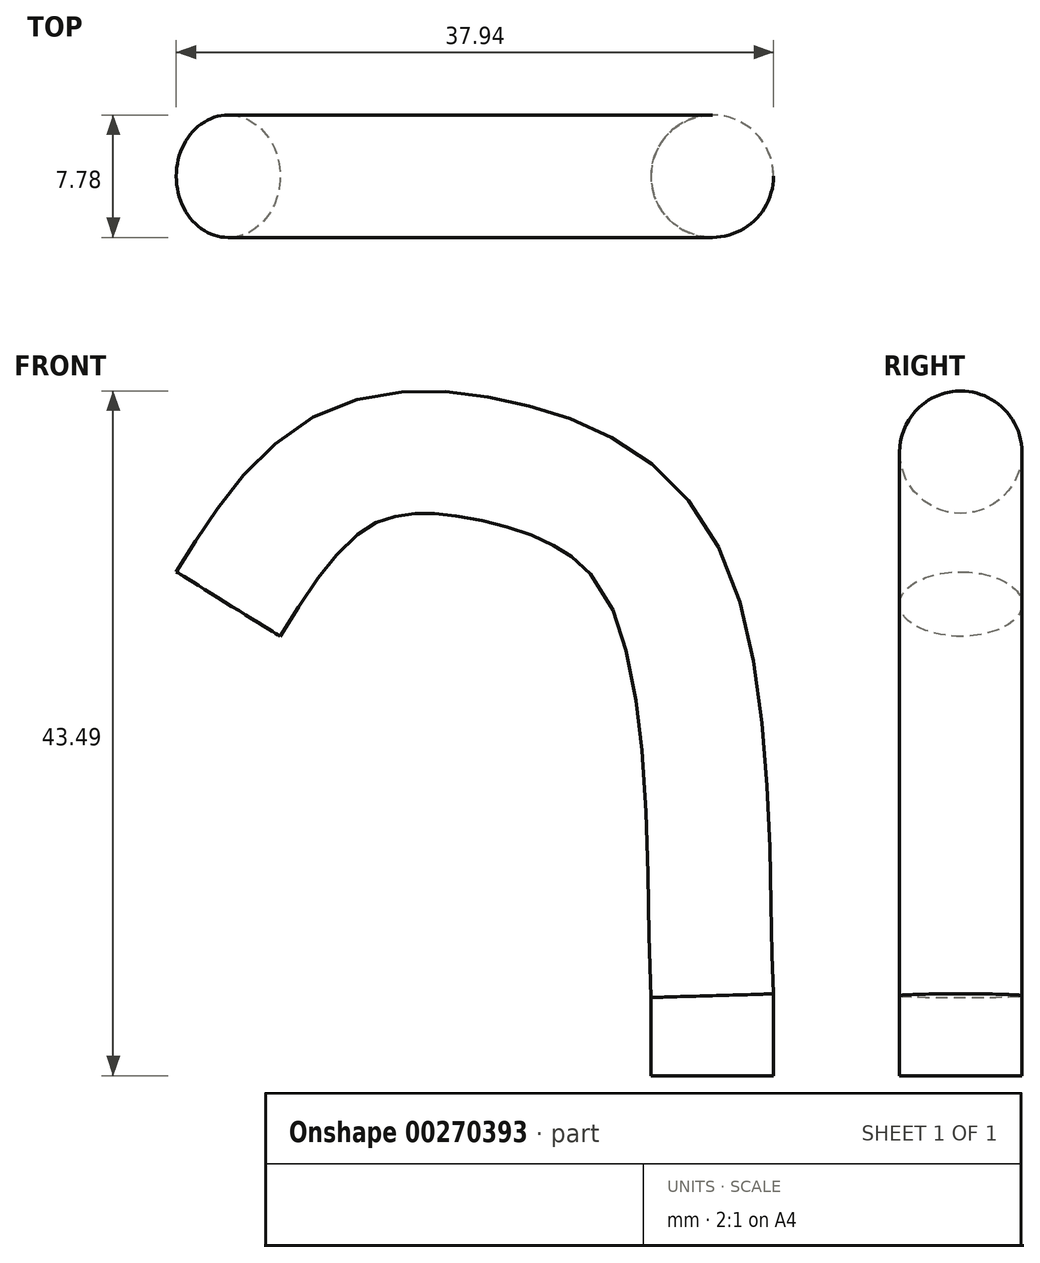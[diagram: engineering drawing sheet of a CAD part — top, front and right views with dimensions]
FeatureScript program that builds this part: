
annotation { "Feature Type Name" : "Feature", "Feature Type Description" : "" }
export const myFeature = defineFeature(function(context is Context, id is Id, definition is map)
    precondition{}
    {
        {
            var Q0;
            Q0=qCreatedBy(makeId("Top.planeOp"),FACE);
            var sketch = newSketch(context, id + "F0", { "sketchPlane" : qUnion([Q0])});
            skCircle(sketch, "E0", {"center": v(0, 0) * mm, "radius": 3.89 * mm});
            skSolve(sketch);
        }
        {
            var Q0;
            Q0=qCreatedBy(makeId("Front.planeOp"),FACE);
            var sketch = newSketch(context, id + "F1", { "sketchPlane" : qUnion([Q0])});
            skLineSegment(sketch, "E1", {"start": v(0, 0) * mm, "end": v(0, 5.08) * mm});
            skFitSpline(sketch, "E2", {"points": [v(0, 5.08) * mm, v(-2.76, 31.14) * mm, v(-12.8, 38.82) * mm, v(-23.45, 38.43) * mm, v(-30.74, 29.95) * mm], "startDerivative": vector(-3.22, 53.86) * mm, "endDerivative": vector(-26.25, -42.31) * mm});
            skSolve(sketch);
        }
        {
            var Q0;
            Q0=makeQuery(id+"F0.imprint","IMPRINT",FACE,{"disambiguationData":[TD([[makeQuery(id+"F0.imprint","IMPRINT",EDGE,{"derivedFrom":sQuery(id+"F0.wireOp",EDGE,"E0")}),1.0]])]});
            var Q1;
            Q1=sQuery(id+"F1.wireOp",EDGE,"E1");
            var Q2;
            Q2=sQuery(id+"F1.wireOp",EDGE,"E2");
            sweep(context, id + "F2", {"profiles" : qUnion([Q0]), "path" : qUnion([Q1, Q2])});
        }
    });
